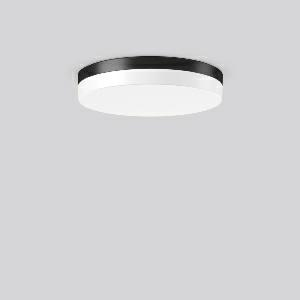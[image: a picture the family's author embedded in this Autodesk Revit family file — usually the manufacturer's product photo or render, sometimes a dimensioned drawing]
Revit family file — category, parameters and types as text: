
# Revit family: flat_slim_round_312632_0031_19_ca4c
name_source: partatom
category: Lighting Fixtures
units: mm (PartAtom-declared; Revit-internal decimal feet)

## family parameters
Cut with Voids When Loaded = No
Host = Face
Light Source = No
Part Type = Normal
Room Calculation Point = No
Round Connector Dimension = Use Diameter
Shared = No

## types (1)
- MultiLumen 1 830 (1 x LED Modul 830, 2400 lm, 3000)
    Apparent Load = 20 VA
    CIE Flux Codes = 39 70 90 83 100
    Color Rendering = 80
    Color Temperature = 3000
    Default Elevation = 1800 mm
    Height = 70 mm
    Lamp = 1 x LED Modul 830
    Lamp Light Flux = 2400 lm
    Lamp count = 1
    Length = 400 mm
    Lifetime = 50000 h
    Luminous efficacy = 120 lm/W
    Manufacturer = RZB
    ModVariant = No
    Model = 312632.0031.19
    Mounting Place = Ceiling
    Mounting Type = Surface mounted
    Number of Poles = 1
    OnlyDefault = Yes
    Power Factor = 1
    Product Name = FLAT SLIM round
    Product group = Surface mounted ceiling and wall luminaires
    ProductGroupID = 305
    Protection Class = Protection class I
    Protection Degree = Degree of protection
    RLX_Detail_Level = 1
    RLX_Emergency_Light_Flux = 0 lm
    RLX_Emergency_Type = 0
    RLX_Emergency_Type_DB = No
    RlxData = <blob elided: 22025 chars, md5=ede08477>
    Socket = socket
    Standby Power = 0 W
    System Light Flux = 2400 lm
    System Power = 20 W
    Type Comments = MultiLumen 1 830
    Type Image = 312631.0031.jpg
    URL = http://relux.com
    VarID = multilumen_1_830
    Voltage = 0 V
    Weight = 0.00 kg
    Width = 0 mm  [stored 0 ft]

note: [stored X ft] marks values corroborated as IEEE doubles in the binary element streams (Revit-internal decimal feet)

## geometry (parser evidence)
native form markers: Blend x4, Sweep x11
no freeform markers — native parametric forms only
